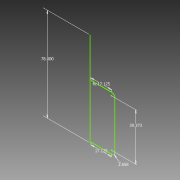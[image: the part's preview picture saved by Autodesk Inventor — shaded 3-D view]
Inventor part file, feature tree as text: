
AUTODESK INVENTOR PART (.ipt)
format: ipt  version: 2013 (Build 170138000, 138)  size: 59,904 bytes
history: native  units: in
note: dims shown in document units (in); Inventor stores cm internally (conversion verified against a paired STEP export)
features: other x1, sketch x1
ambient origin geometry x8: Origin, YZ Plane, XZ Plane, XY Plane, X Axis, Y Axis, Z Axis, Center Point
feature tree (2):
  other  "FE00036LowerFrame.ipt"
  sketch  "Sketch1"  dims[d0=0.3937in d8=2.6575in d9=39.828in d10=17.125in d11=17.125in]
